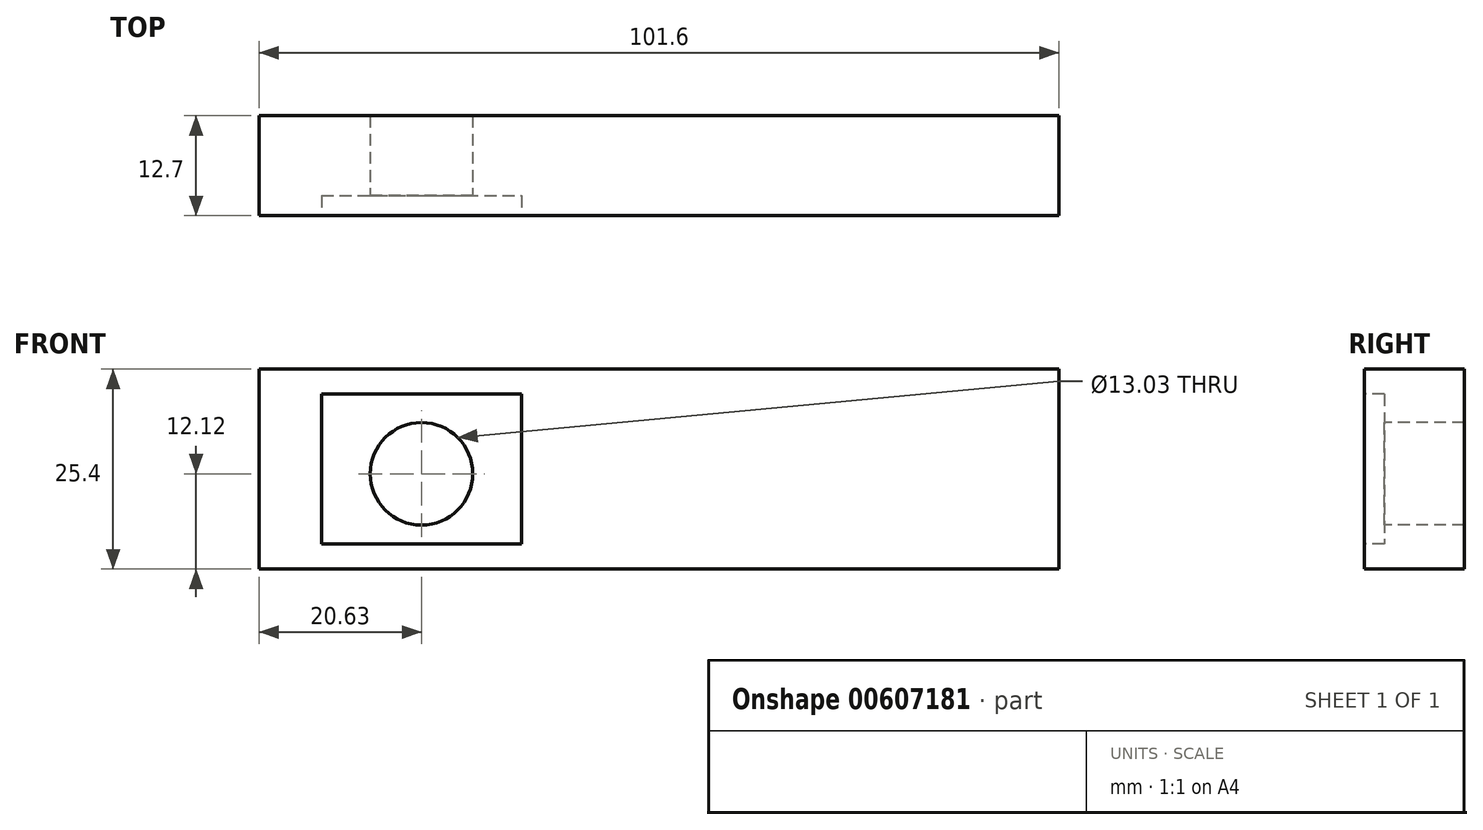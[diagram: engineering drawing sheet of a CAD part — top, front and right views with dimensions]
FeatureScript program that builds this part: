
annotation { "Feature Type Name" : "Feature", "Feature Type Description" : "" }
export const myFeature = defineFeature(function(context is Context, id is Id, definition is map)
    precondition{}
    {
        {
            var Q0;
            Q0=qCreatedBy(makeId("Front.planeOp"),FACE);
            var sketch = newSketch(context, id + "F0", { "sketchPlane" : qUnion([Q0])});
            skLineSegment(sketch, "E0.bottom", {"start": v(-33.33, 13.28) * mm, "end": v(68.27, 13.28) * mm});
            skLineSegment(sketch, "E0.top", {"start": v(-33.33, -12.12) * mm, "end": v(68.27, -12.12) * mm});
            skLineSegment(sketch, "E0.left", {"start": v(-33.33, 13.28) * mm, "end": v(-33.33, -12.12) * mm});
            skLineSegment(sketch, "E0.right", {"start": v(68.27, 13.28) * mm, "end": v(68.27, -12.12) * mm});
            skSolve(sketch);
        }
        {
            var Q0;
            Q0=makeQuery(id+"F0.imprint","IMPRINT",FACE,{"disambiguationData":[TD([[makeQuery(id+"F0.imprint","IMPRINT",EDGE,{"derivedFrom":sQuery(id+"F0.wireOp",EDGE,"E0.bottom")}),-1.0]])]});
            extrude(context, id + "F1", {"entities" : qUnion([Q0]), "depth" : 12.7 * mm, "offsetDistance" : 25.4 * mm});
        }
        {
            var Q0;
            Q0=makeQuery(id+"F1.opExtrude","CAP_FACE",FACE,{"disambiguationData":[OSD([sQuery(id+"F0.wireOp",EDGE,"E0.bottom"),sQuery(id+"F0.wireOp",EDGE,"E0.top"),sQuery(id+"F0.wireOp",EDGE,"E0.left"),sQuery(id+"F0.wireOp",EDGE,"E0.right")])],"isStart":false});
            var sketch = newSketch(context, id + "F2", { "sketchPlane" : qUnion([Q0])});
            skLineSegment(sketch, "E1.bottom", {"start": v(-25.4, 10.1) * mm, "end": v(0, 10.1) * mm});
            skLineSegment(sketch, "E1.top", {"start": v(-25.4, -8.94) * mm, "end": v(0, -8.94) * mm});
            skLineSegment(sketch, "E1.left", {"start": v(-25.4, 10.1) * mm, "end": v(-25.4, -8.94) * mm});
            skLineSegment(sketch, "E1.right", {"start": v(0, 10.1) * mm, "end": v(0, -8.94) * mm});
            skSolve(sketch);
        }
        {
            var Q0;
            Q0=makeQuery(id+"F2.imprint","IMPRINT",FACE,{"disambiguationData":[TD([[makeQuery(id+"F2.imprint","IMPRINT",EDGE,{"derivedFrom":sQuery(id+"F2.wireOp",EDGE,"E1.bottom")}),-1.0]])]});
            extrude(context, id + "F3", {"entities" : qUnion([Q0]), "operationType" : NewBodyOperationType.REMOVE, "oppositeDirection" : true, "depth" : 2.54 * mm, "offsetDistance" : 25.4 * mm});
        }
        {
            var Q0;
            Q0=makeQuery(id+"F3.boolean.opBoolean","COPY",FACE,{"derivedFrom":makeQuery(id+"F3.opExtrude","CAP_FACE",FACE,{"disambiguationData":[OSD([sQuery(id+"F2.wireOp",EDGE,"E1.bottom"),sQuery(id+"F2.wireOp",EDGE,"E1.top"),sQuery(id+"F2.wireOp",EDGE,"E1.left"),sQuery(id+"F2.wireOp",EDGE,"E1.right")])],"isStart":false})});
            var sketch = newSketch(context, id + "F4", { "sketchPlane" : qUnion([Q0])});
            skLineSegment(sketch, "E2", {"start": v(0, 0) * mm, "end": v(-25.4, 0) * mm});
            skCircle(sketch, "E3", {"center": v(-12.7, 0) * mm, "radius": 6.51 * mm});
            skSolve(sketch);
        }
        {
            var Q0;
            {var subQ0=sQuery(id+"F4.wireOp",EDGE,"E3");var subQ1=sQuery(id+"F4.wireOp",EDGE,"E2");var subQ2=makeQuery(id+"F4.imprint","INTERSECT",VERTEX,{"disambiguationData":[OD(0.0)],"derivedFrom":[subQ1,subQ0]});Q0=makeQuery(id+"F4.imprint","IMPRINT",FACE,{"disambiguationData":[TD([[makeQuery(id+"F4.imprint","IMPRINT",EDGE,{"disambiguationData":[TD([[subQ2,-1.0]])],"derivedFrom":subQ1}),1.0]])]});}
            var Q1;
            {var subQ0=sQuery(id+"F4.wireOp",EDGE,"E3");var subQ1=sQuery(id+"F4.wireOp",EDGE,"E2");var subQ2=makeQuery(id+"F4.imprint","INTERSECT",VERTEX,{"disambiguationData":[OD(0.0)],"derivedFrom":[subQ1,subQ0]});Q1=makeQuery(id+"F4.imprint","IMPRINT",FACE,{"disambiguationData":[TD([[makeQuery(id+"F4.imprint","IMPRINT",EDGE,{"disambiguationData":[TD([[subQ2,-1.0]])],"derivedFrom":subQ1}),-1.0]])]});}
            extrude(context, id + "F5", {"entities" : qUnion([Q0, Q1]), "operationType" : NewBodyOperationType.REMOVE, "oppositeDirection" : true, "depth" : 25.4 * mm, "offsetDistance" : 25.4 * mm});
        }
    });
